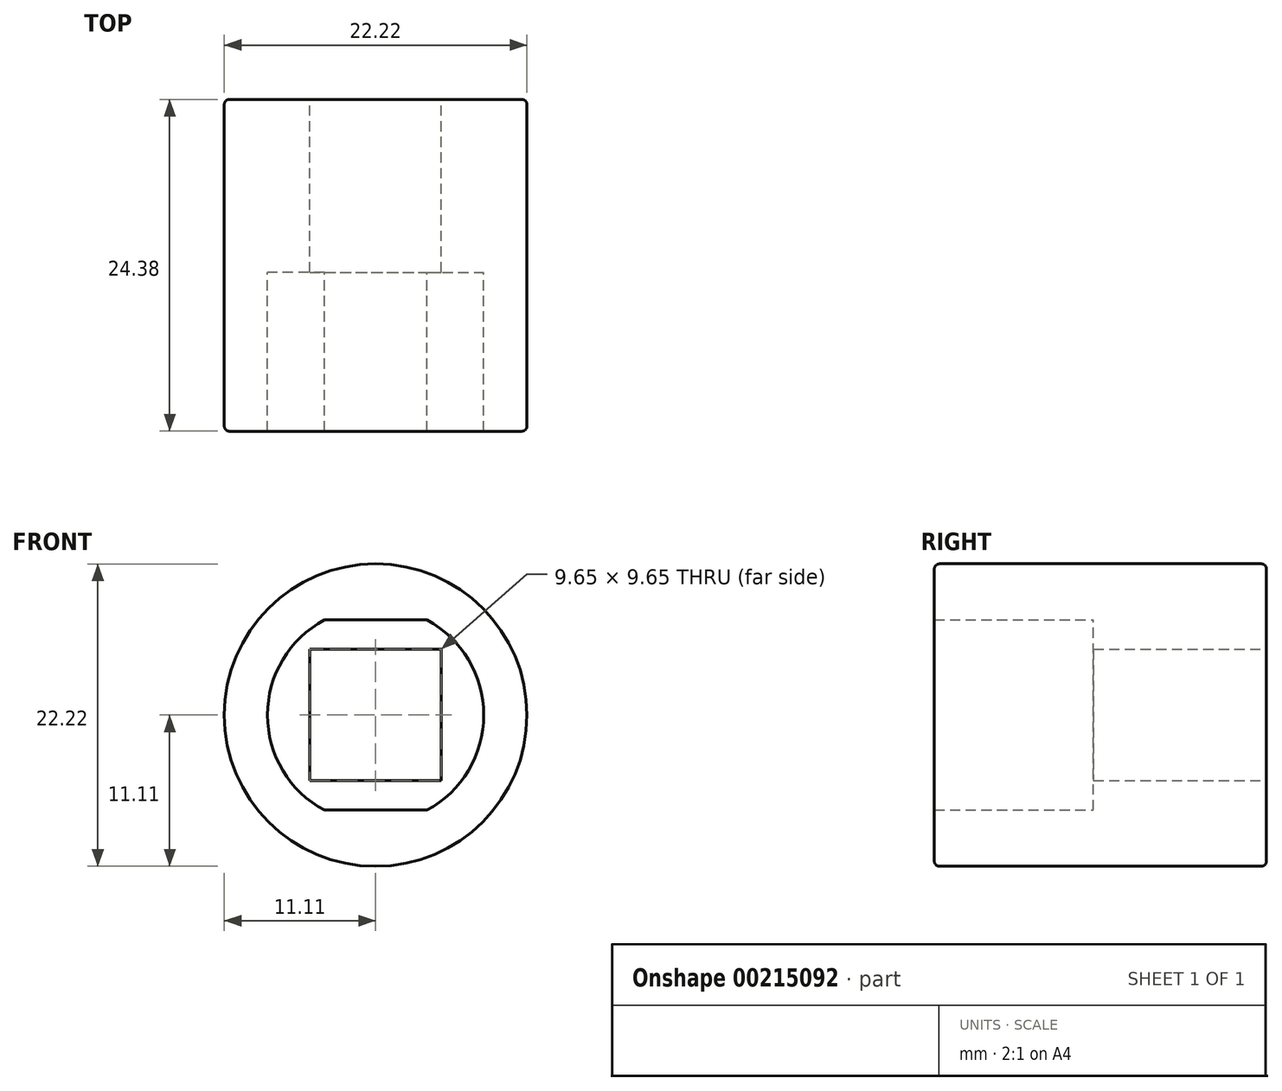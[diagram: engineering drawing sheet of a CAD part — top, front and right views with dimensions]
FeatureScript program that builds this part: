
annotation { "Feature Type Name" : "Feature", "Feature Type Description" : "" }
export const myFeature = defineFeature(function(context is Context, id is Id, definition is map)
    precondition{}
    {
        {
            var Q0;
            Q0=qCreatedBy(makeId("Front.planeOp"),FACE);
            var sketch = newSketch(context, id + "F0", { "sketchPlane" : qUnion([Q0])});
            skCircle(sketch, "E0", {"center": v(0, 0) * mm, "radius": 7.94 * mm});
            skLineSegment(sketch, "E1", {"start": v(-3.77, 6.99) * mm, "end": v(3.77, 6.99) * mm});
            skLineSegment(sketch, "E2", {"start": v(-3.77, -6.99) * mm, "end": v(3.77, -6.99) * mm});
            skArc(sketch, "E3", {"start": v(-3.77, 6.99) * mm, "mid": v(-7.94, 0) * mm, "end": v(-3.77, -6.99) * mm});
            skArc(sketch, "E4", {"start": v(3.77, 6.99) * mm, "mid": v(7.94, 0) * mm, "end": v(3.77, -6.99) * mm});
            skCircle(sketch, "E5", {"center": v(0, 0) * mm, "radius": 11.11 * mm});
            skLineSegment(sketch, "E6.bottom", {"start": v(-4.83, 4.83) * mm, "end": v(4.83, 4.83) * mm});
            skLineSegment(sketch, "E6.top", {"start": v(-4.83, -4.83) * mm, "end": v(4.83, -4.83) * mm});
            skLineSegment(sketch, "E6.left", {"start": v(-4.83, 4.83) * mm, "end": v(-4.83, -4.83) * mm});
            skLineSegment(sketch, "E6.right", {"start": v(4.83, 4.83) * mm, "end": v(4.83, -4.83) * mm});
            skSolve(sketch);
        }
        {
            var Q0;
            Q0=makeQuery(id+"F0.imprint","IMPRINT",FACE,{"disambiguationData":[TD([[makeQuery(id+"F0.imprint","IMPRINT",EDGE,{"derivedFrom":sQuery(id+"F0.wireOp",EDGE,"E5")}),1.0]])]});
            var Q1;
            {var subQ0=sQuery(id+"F0.wireOp",EDGE,"E2");Q1=makeQuery(id+"F0.imprint","IMPRINT",FACE,{"disambiguationData":[TD([[makeQuery(id+"F0.imprint","IMPRINT",EDGE,{"derivedFrom":subQ0}),-1.0]])]});}
            var Q2;
            {var subQ0=sQuery(id+"F0.wireOp",EDGE,"E1");Q2=makeQuery(id+"F0.imprint","IMPRINT",FACE,{"disambiguationData":[TD([[makeQuery(id+"F0.imprint","IMPRINT",EDGE,{"derivedFrom":subQ0}),1.0]])]});}
            extrude(context, id + "F1", {"entities" : qUnion([Q0, Q1, Q2]), "depth" : 24.38 * mm});
        }
        {
            var Q0;
            {var subQ1=sQuery(id+"F0.wireOp",EDGE,"E1");Q0=makeQuery(id+"F0.imprint","IMPRINT",FACE,{"disambiguationData":[TD([[makeQuery(id+"F0.imprint","IMPRINT",EDGE,{"derivedFrom":subQ1}),-1.0]])]});}
            extrude(context, id + "F2", {"entities" : qUnion([Q0]), "operationType" : NewBodyOperationType.ADD, "depth" : 12.7 * mm});
        }
        {
            var Q0;
            Q0=makeQuery(id+"F1.opExtrude","CAP_EDGE",EDGE,{"disambiguationData":[OSD([sQuery(id+"F0.wireOp",EDGE,"E5")])],"isStart":false});
            var Q1;
            Q1=makeQuery(id+"F1.opExtrude","CAP_EDGE",EDGE,{"disambiguationData":[OSD([sQuery(id+"F0.wireOp",EDGE,"E5")])],"isStart":true});
            fillet(context, id + "F3", {"entities" : qUnion([Q0, Q1]), "radius" : 0.38 * mm, "tangentPropagation" : true, "allowEdgeOverflow" : false});
        }
    });
